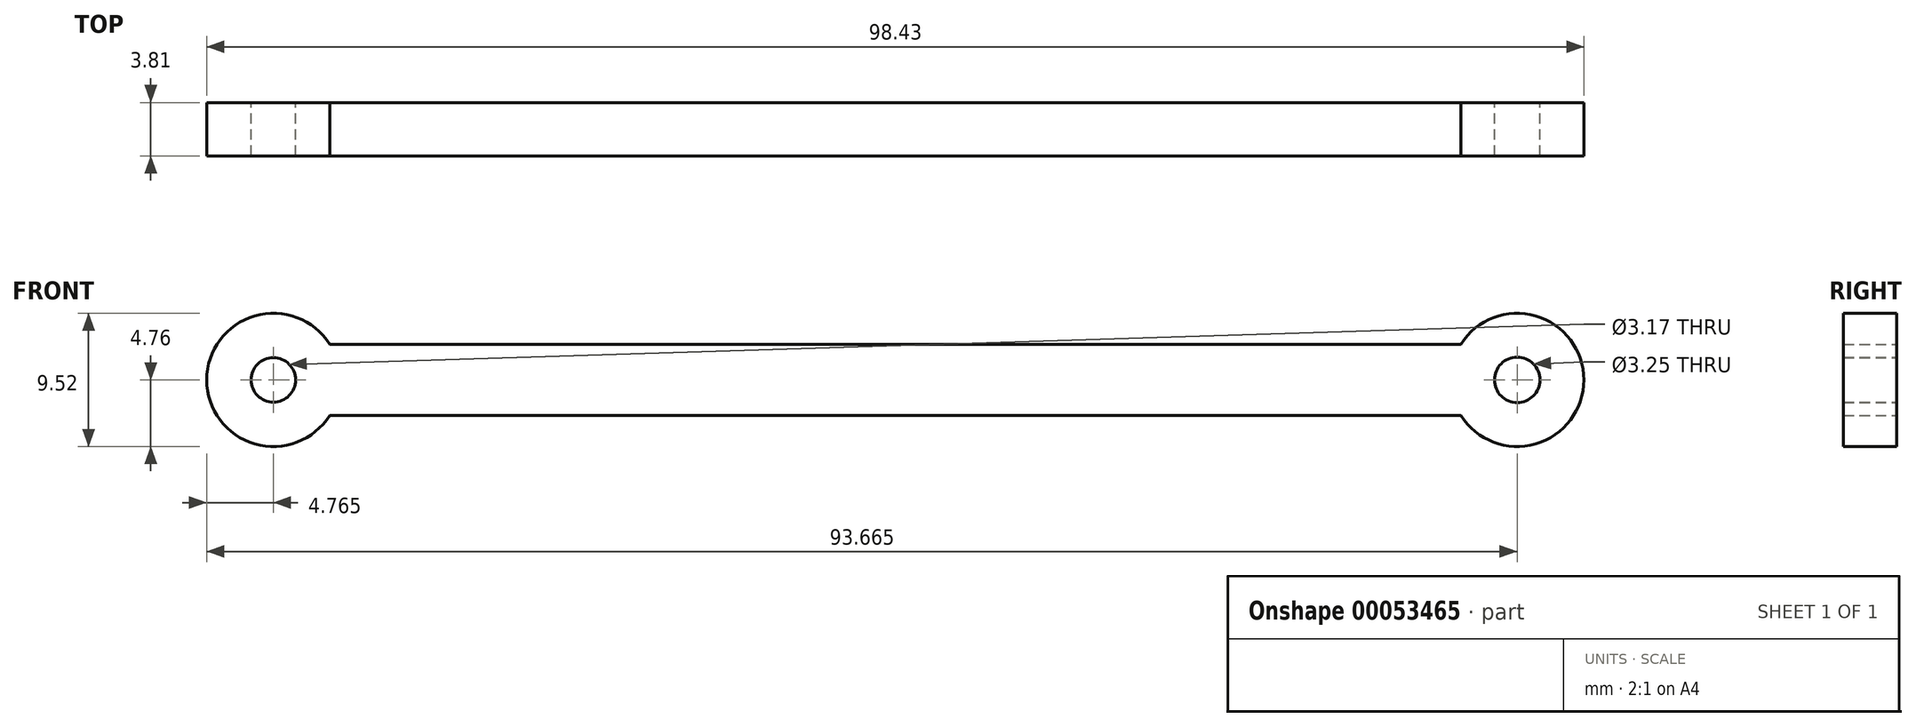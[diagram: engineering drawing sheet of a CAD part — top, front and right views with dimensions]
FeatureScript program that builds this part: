
annotation { "Feature Type Name" : "Feature", "Feature Type Description" : "" }
export const myFeature = defineFeature(function(context is Context, id is Id, definition is map)
    precondition{}
    {
        {
            var Q0;
            Q0=qCreatedBy(makeId("Front.planeOp"),FACE);
            var sketch = newSketch(context, id + "F0", { "sketchPlane" : qUnion([Q0])});
            skArc(sketch, "E0", {"start": v(-37.62, 2.54) * mm, "mid": v(-46.4, 0) * mm, "end": v(-37.62, -2.54) * mm});
            skArc(sketch, "E1", {"start": v(43.23, -2.54) * mm, "mid": v(52.02, 0) * mm, "end": v(43.23, 2.54) * mm});
            skLineSegment(sketch, "E2", {"start": v(-37.62, 2.54) * mm, "end": v(43.23, 2.54) * mm});
            skLineSegment(sketch, "E3", {"start": v(43.23, -2.54) * mm, "end": v(-37.62, -2.54) * mm});
            skCircle(sketch, "E4", {"center": v(-41.65, 0) * mm, "radius": 1.59 * mm});
            skCircle(sketch, "E5", {"center": v(47.25, 0) * mm, "radius": 1.63 * mm});
            skSolve(sketch);
        }
        {
            var Q0;
            Q0 = qSketchRegion(id + "F0", true);
            extrude(context, id + "F1", {"entities" : qUnion([Q0]), "depth" : 3.8 * mm});
        }
    });
